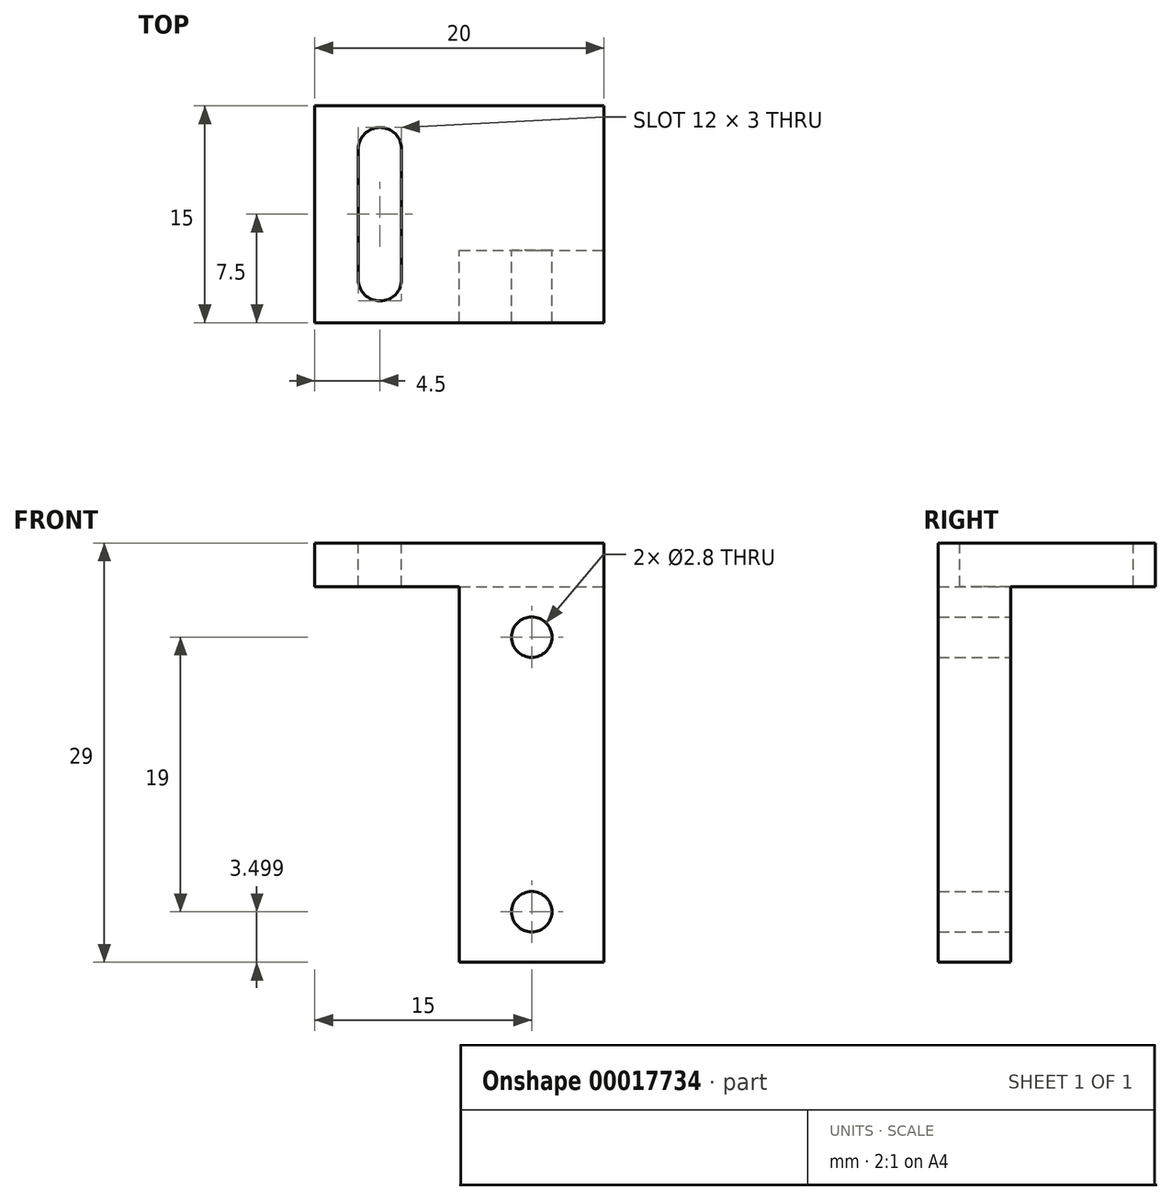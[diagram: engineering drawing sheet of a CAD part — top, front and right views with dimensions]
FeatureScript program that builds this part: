
annotation { "Feature Type Name" : "Feature", "Feature Type Description" : "" }
export const myFeature = defineFeature(function(context is Context, id is Id, definition is map)
    precondition{}
    {
        {
            var Q0;
            Q0=qCreatedBy(makeId("Front.planeOp"),FACE);
            var sketch = newSketch(context, id + "F0", { "sketchPlane" : qUnion([Q0])});
            skLineSegment(sketch, "E0.bottom", {"start": v(-2.41, 8.63) * mm, "end": v(7.59, 8.63) * mm});
            skLineSegment(sketch, "E0.top", {"start": v(-2.41, -20.37) * mm, "end": v(7.59, -20.37) * mm});
            skLineSegment(sketch, "E0.left", {"start": v(-2.41, 8.63) * mm, "end": v(-2.41, -20.37) * mm});
            skLineSegment(sketch, "E0.right", {"start": v(7.59, 8.63) * mm, "end": v(7.59, -20.37) * mm});
            skLineSegment(sketch, "E1.0", {"start": v(-2.41, 5.63) * mm, "end": v(5.59, 5.63) * mm, "construction": true});
            skSolve(sketch);
        }
        {
            var Q0;
            Q0=makeQuery(id+"F0.imprint","IMPRINT",FACE,{"disambiguationData":[TD([[makeQuery(id+"F0.imprint","IMPRINT",EDGE,{"derivedFrom":sQuery(id+"F0.wireOp",EDGE,"E0.bottom")}),-1.0]])]});
            extrude(context, id + "F1", {"entities" : qUnion([Q0]), "depth" : 5 * mm});
        }
        {
            var Q0;
            Q0=makeQuery(id+"F1.opExtrude","CAP_FACE",FACE,{"disambiguationData":[OSD([sQuery(id+"F0.wireOp",EDGE,"E0.bottom"),sQuery(id+"F0.wireOp",EDGE,"E0.top"),sQuery(id+"F0.wireOp",EDGE,"E0.left"),sQuery(id+"F0.wireOp",EDGE,"E0.right")])],"isStart":true});
            var sketch = newSketch(context, id + "F2", { "sketchPlane" : qUnion([Q0])});
            skLineSegment(sketch, "E2.0", {"start": v(-2.59, 9.63) * mm, "end": v(-2.59, -20.37) * mm, "construction": true});
            skCircle(sketch, "E3", {"center": v(-2.59, 2.13) * mm, "radius": 1.4 * mm});
            skCircle(sketch, "E4", {"center": v(-2.59, -16.87) * mm, "radius": 1.4 * mm});
            skLineSegment(sketch, "E5.0", {"start": v(2.41, -16.87) * mm, "end": v(-7.59, -16.87) * mm, "construction": true});
            skLineSegment(sketch, "E6.0", {"start": v(2.41, 2.13) * mm, "end": v(-7.59, 2.13) * mm, "construction": true});
            skSolve(sketch);
        }
        {
            var Q0;
            Q0 = qSketchRegion(id + "F2", true);
            extrude(context, id + "F3", {"entities" : qUnion([Q0]), "operationType" : NewBodyOperationType.REMOVE, "oppositeDirection" : true, "depth" : 25 * mm});
        }
        {
            var Q0;
            Q0=makeQuery(id+"F1.opExtrude","SWEPT_FACE",FACE,{"disambiguationData":[OSD([sQuery(id+"F0.wireOp",EDGE,"E0.left")])]});
            var sketch = newSketch(context, id + "F4", { "sketchPlane" : qUnion([Q0])});
            skLineSegment(sketch, "E7.0", {"start": v(5, 5.63) * mm, "end": v(0, 5.63) * mm});
            skSolve(sketch);
        }
        {
            var Q0;
            Q0 = qSketchRegion(id + "F4", true);
            var Q1;
            {var subQ2=sQuery(id+"F4.wireOp",EDGE,"E7.0");Q1=makeQuery(id+"F4.imprint","IMPRINT",FACE,{"disambiguationData":[TD([[makeQuery(id+"F4.imprint","IMPRINT",EDGE,{"derivedFrom":subQ2}),-1.0]])]});}
            extrude(context, id + "F5", {"entities" : qUnion([Q0, Q1]), "operationType" : NewBodyOperationType.ADD, "depth" : 10 * mm});
        }
        {
            var Q0;
            {var subQ0=sQuery(id+"F0.wireOp",EDGE,"E0.bottom");var subQ1=sQuery(id+"F0.wireOp",EDGE,"E0.left");var subQ2=makeQuery(id+"F1.opExtrude","CAP_EDGE",EDGE,{"disambiguationData":[OSD([subQ1])],"isStart":false});Q0=makeQuery(id+"F5.boolean.opBoolean","MERGE",FACE,{"derivedFrom":[makeQuery(id+"F1.opExtrude","CAP_FACE",FACE,{"disambiguationData":[OSD([subQ0,sQuery(id+"F0.wireOp",EDGE,"E0.top"),subQ1,sQuery(id+"F0.wireOp",EDGE,"E0.right")])],"isStart":false}),makeQuery(id+"F5.opExtrude","SWEPT_FACE",FACE,{"disambiguationData":[OSD([subQ1]),TDD([makeQuery(id+"F4.imprint","IMPRINT",EDGE,{"disambiguationData":[TD([[makeQuery(id+"F4.imprint","INTERSECT",VERTEX,{"derivedFrom":[subQ2,sQuery(id+"F4.wireOp",EDGE,"E7.0")]}),1.0]])],"derivedFrom":subQ2})])]})]});}
            var sketch = newSketch(context, id + "F6", { "sketchPlane" : qUnion([Q0])});
            skLineSegment(sketch, "E8", {"start": v(-2.41, 5.63) * mm, "end": v(7.59, 5.63) * mm});
            skSolve(sketch);
        }
        {
            var Q0;
            {var subQ1=sQuery(id+"F6.wireOp",EDGE,"E8");Q0=makeQuery(id+"F6.imprint","IMPRINT",FACE,{"disambiguationData":[TD([[makeQuery(id+"F6.imprint","IMPRINT",EDGE,{"derivedFrom":subQ1}),1.0]])]});}
            extrude(context, id + "F7", {"entities" : qUnion([Q0]), "operationType" : NewBodyOperationType.ADD, "oppositeDirection" : true, "depth" : 15 * mm});
        }
        {
            var Q0;
            {var subQ0=sQuery(id+"F0.wireOp",EDGE,"E0.bottom");var subQ1=sQuery(id+"F0.wireOp",EDGE,"E0.left");Q0=makeQuery(id+"F7.boolean.opBoolean","MERGE",FACE,{"derivedFrom":[makeQuery(id+"F5.boolean.opBoolean","MERGE",FACE,{"derivedFrom":[makeQuery(id+"F1.opExtrude","SWEPT_FACE",FACE,{"disambiguationData":[OSD([subQ0])]}),makeQuery(id+"F5.opExtrude","SWEPT_FACE",FACE,{"disambiguationData":[OSD([subQ0,subQ1])]})]}),makeQuery(id+"F7.opExtrude","SWEPT_FACE",FACE,{"disambiguationData":[OSD([subQ0,subQ1])]})]});}
            var sketch = newSketch(context, id + "F8", { "sketchPlane" : qUnion([Q0])});
            skLineSegment(sketch, "E9.0", {"start": v(-7.91, -10) * mm, "end": v(-7.91, 13.41) * mm, "construction": true});
            skLineSegment(sketch, "E10.0", {"start": v(-6.41, -2) * mm, "end": v(-6.41, 7) * mm});
            skLineSegment(sketch, "E11.0", {"start": v(-9.41, -2) * mm, "end": v(-9.41, 7) * mm});
            skLineSegment(sketch, "E12.0", {"start": v(-12.41, 7) * mm, "end": v(7.59, 7) * mm, "construction": true});
            skLineSegment(sketch, "E13.0", {"start": v(-12.41, -2) * mm, "end": v(7.59, -2) * mm, "construction": true});
            skArc(sketch, "E14", {"start": v(-9.41, 7) * mm, "mid": v(-7.91, 8.5) * mm, "end": v(-6.41, 7) * mm});
            skArc(sketch, "E15", {"start": v(-6.41, -2) * mm, "mid": v(-7.91, -3.5) * mm, "end": v(-9.41, -2) * mm});
            skSolve(sketch);
        }
        {
            var Q0;
            Q0=makeQuery(id+"F8.imprint","IMPRINT",FACE,{"disambiguationData":[TD([[makeQuery(id+"F8.imprint","IMPRINT",EDGE,{"derivedFrom":sQuery(id+"F8.wireOp",EDGE,"a678a36d-41d2-427d-8e55-0325338021f2.0")}),1.0]])]});
            var Q1;
            Q1=makeQuery(id+"F8.imprint","IMPRINT",FACE,{"disambiguationData":[TD([[makeQuery(id+"F8.imprint","IMPRINT",EDGE,{"derivedFrom":sQuery(id+"F8.wireOp",EDGE,"E10.0")}),1.0]])]});
            var Q2;
            Q2=sQuery(id+"F8.wireOp",EDGE,"a3b55649-b8dd-449b-a23e-8d3800de4019");
            var Q3;
            Q3=sQuery(id+"F8.wireOp",EDGE,"a678a36d-41d2-427d-8e55-0325338021f2.1");
            var Q4;
            Q4=sQuery(id+"F8.wireOp",EDGE,"a678a36d-41d2-427d-8e55-0325338021f2.0");
            var Q5;
            Q5=sQuery(id+"F8.wireOp",EDGE,"b0d7fb9c-0a67-47c0-9b60-9e4a61582d00");
            var Q6;
            Q6=sQuery(id+"F8.wireOp",EDGE,"8b5e1ef5-08ee-4b97-a625-3d02ef5d0c2a.0");
            var Q7;
            Q7=sQuery(id+"F8.wireOp",EDGE,"718d5cb8-3b57-48ea-b748-e179312c4179.0");
            extrude(context, id + "F9", {"entities" : qUnion([Q0, Q1]), "operationType" : NewBodyOperationType.REMOVE, "surfaceEntities" : qUnion([Q2, Q3, Q4, Q5, Q6, Q7]), "oppositeDirection" : true, "depth" : 25 * mm});
        }
    });
